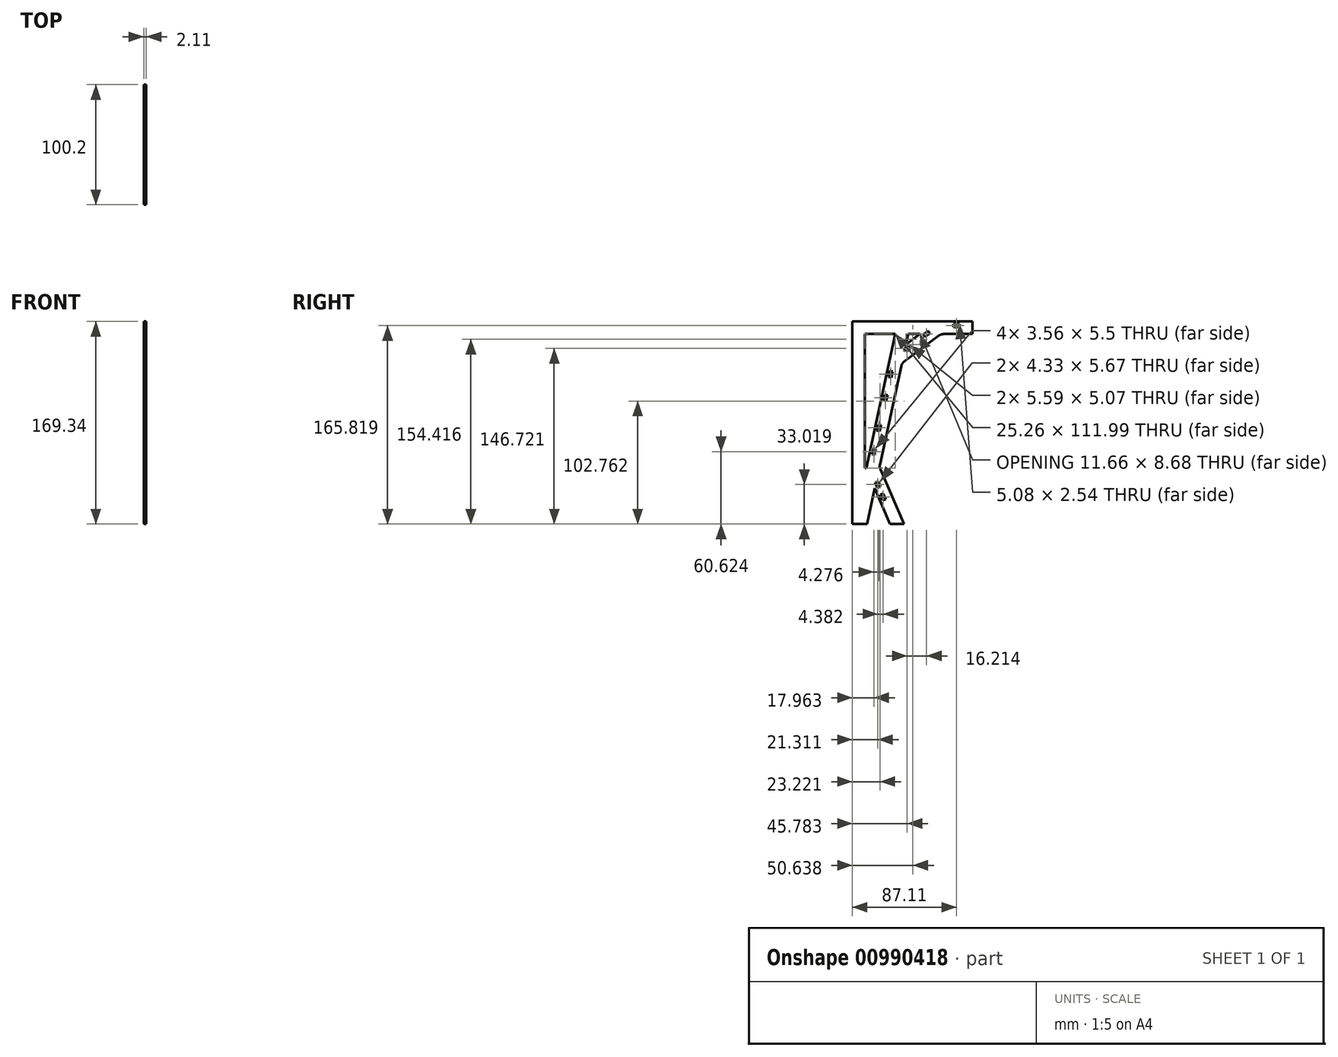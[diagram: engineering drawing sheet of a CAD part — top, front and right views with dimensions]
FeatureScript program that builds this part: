
annotation { "Feature Type Name" : "Feature", "Feature Type Description" : "" }
export const myFeature = defineFeature(function(context is Context, id is Id, definition is map)
    precondition{}
    {
        {
            var Q0;
            Q0=qCreatedBy(makeId("Right.planeOp"),FACE);
            var sketch = newSketch(context, id + "F0", { "sketchPlane" : qUnion([Q0])});
            skLineSegment(sketch, "E0", {"start": v(0, 0) * mm, "end": v(0, 169.34) * mm});
            skLineSegment(sketch, "E1", {"start": v(0, 169.34) * mm, "end": v(200.4, 169.34) * mm});
            skLineSegment(sketch, "E2", {"start": v(0, 0) * mm, "end": v(43.05, 0) * mm, "construction": true});
            skLineSegment(sketch, "E3", {"start": v(43.05, 0) * mm, "end": v(23.47, 45.96) * mm});
            skLineSegment(sketch, "E4", {"start": v(0, 47.82) * mm, "end": v(22.68, 47.82) * mm, "construction": true});
            skLineSegment(sketch, "E5", {"start": v(22.68, 47.82) * mm, "end": v(22.68, 0) * mm, "construction": true});
            skLineSegment(sketch, "E6", {"start": v(23.1, 49.8) * mm, "end": v(40.9, 132) * mm});
            skLineSegment(sketch, "E7", {"start": v(41.4, 134.33) * mm, "end": v(0, 134.33) * mm, "construction": true});
            skLineSegment(sketch, "E8", {"start": v(41.4, 134.33) * mm, "end": v(43.05, 0) * mm, "construction": true});
            skLineSegment(sketch, "E9", {"start": v(43.31, 135.75) * mm, "end": v(72.51, 157.5) * mm});
            skLineSegment(sketch, "E10", {"start": v(74.2, 158.76) * mm, "end": v(74.2, 169.34) * mm, "construction": true});
            skLineSegment(sketch, "E11", {"start": v(74.2, 158.76) * mm, "end": v(0, 158.76) * mm, "construction": true});
            skPoint(sketch, "E12", {"position": v(100.2, 169.34) * mm});
            skLineSegment(sketch, "E13", {"start": v(100.2, 169.34) * mm, "end": v(100.2, 154.3) * mm, "construction": true});
            skLineSegment(sketch, "E14", {"start": v(76.3, 158.76) * mm, "end": v(100.2, 158.76) * mm});
            skLineSegment(sketch, "E15.4", {"start": v(41.18, -0.8) * mm, "end": v(20.56, 47.62) * mm, "construction": true});
            skLineSegment(sketch, "E15.5", {"start": v(20.56, 47.62) * mm, "end": v(39.58, 135.5) * mm});
            skLineSegment(sketch, "E15.6", {"start": v(39.58, 135.5) * mm, "end": v(73.52, 160.79) * mm});
            skLineSegment(sketch, "E15.7", {"start": v(73.52, 160.79) * mm, "end": v(100.2, 160.79) * mm});
            skLineSegment(sketch, "E16.5", {"start": v(11.62, 46.77) * mm, "end": v(31.89, 140.45) * mm});
            skLineSegment(sketch, "E16.6", {"start": v(31.89, 140.45) * mm, "end": v(70.69, 169.35) * mm, "construction": true});
            skLineSegment(sketch, "E16.7", {"start": v(70.69, 169.35) * mm, "end": v(100.2, 169.35) * mm});
            skLineSegment(sketch, "E17", {"start": v(31.89, 140.45) * mm, "end": v(38.14, 169.34) * mm, "construction": true});
            skLineSegment(sketch, "E18", {"start": v(10.6, 158.76) * mm, "end": v(0, 158.76) * mm, "construction": true});
            skLineSegment(sketch, "E19", {"start": v(10.6, 158.76) * mm, "end": v(10.6, 46.77) * mm});
            skLineSegment(sketch, "E20", {"start": v(10.6, 46.77) * mm, "end": v(11.62, 46.77) * mm});
            skLineSegment(sketch, "E21", {"start": v(36.3, 160.79) * mm, "end": v(31.89, 140.45) * mm, "construction": true});
            skLineSegment(sketch, "E22", {"start": v(41.4, 134.33) * mm, "end": v(48.98, 169.34) * mm, "construction": true});
            skLineSegment(sketch, "E23", {"start": v(47.13, 160.79) * mm, "end": v(44.8, 150.07) * mm});
            skLineSegment(sketch, "E24", {"start": v(13.2, 0) * mm, "end": v(0, 0) * mm});
            skLineSegment(sketch, "E25", {"start": v(31.54, 0) * mm, "end": v(43.05, 0) * mm});
            skLineSegment(sketch, "E26", {"start": v(100.2, 158.76) * mm, "end": v(100.2, 169.35) * mm});
            skPoint(sketch, "E27", {"position": v(46.69, 158.76) * mm});
            skPoint(sketch, "E28", {"position": v(56.47, 158.76) * mm});
            skLineSegment(sketch, "E29", {"start": v(46.69, 158.76) * mm, "end": v(56.47, 158.76) * mm});
            skLineSegment(sketch, "E30", {"start": v(44.8, 150.07) * mm, "end": v(46.69, 158.76) * mm});
            skLineSegment(sketch, "E31", {"start": v(10.6, 158.76) * mm, "end": v(35.85, 158.76) * mm});
            skLineSegment(sketch, "E32", {"start": v(35.85, 158.76) * mm, "end": v(31.89, 140.45) * mm});
            skLineSegment(sketch, "E33", {"start": v(44.8, 150.07) * mm, "end": v(56.47, 158.76) * mm});
            skLineSegment(sketch, "E34", {"start": v(30.88, 85.7) * mm, "end": v(20.53, 87.94) * mm, "construction": true});
            skLineSegment(sketch, "E35.0", {"start": v(33.3, -4.15) * mm, "end": v(12.94, 43.67) * mm, "construction": true});
            skLineSegment(sketch, "E36", {"start": v(22.68, 47.82) * mm, "end": v(18.8, 29.9) * mm, "construction": true});
            skLineSegment(sketch, "E37", {"start": v(18.8, 29.9) * mm, "end": v(12.34, 0) * mm});
            skLineSegment(sketch, "E38", {"start": v(18.8, 29.9) * mm, "end": v(31.54, 0) * mm});
            skLineSegment(sketch, "E39", {"start": v(12.34, 0) * mm, "end": v(31.54, 0) * mm});
            skLineSegment(sketch, "E40", {"start": v(20.56, 47.62) * mm, "end": v(40.84, 0) * mm});
            skPoint(sketch, "E41.visualSharp", {"position": v(41.4, 134.33) * mm});
            skArc(sketch, "E41.filletArc", {"start": v(43.31, 135.75) * mm, "mid": v(41.77, 134.1) * mm, "end": v(40.9, 132) * mm});
            skPoint(sketch, "E42.visualSharp", {"position": v(22.68, 47.82) * mm});
            skArc(sketch, "E42.filletArc", {"start": v(23.1, 49.8) * mm, "mid": v(23, 47.85) * mm, "end": v(23.47, 45.96) * mm});
            skPoint(sketch, "E43.visualSharp", {"position": v(74.2, 158.76) * mm});
            skArc(sketch, "E43.filletArc", {"start": v(76.3, 158.76) * mm, "mid": v(74.3, 158.44) * mm, "end": v(72.51, 157.5) * mm});
            skPoint(sketch, "E44", {"position": v(21.75, 93.6) * mm});
            skLineSegment(sketch, "E45", {"start": v(21.75, 93.6) * mm, "end": v(22.1, 95.21) * mm});
            skLineSegment(sketch, "E46", {"start": v(22.1, 95.21) * mm, "end": v(26.54, 94.25) * mm});
            skLineSegment(sketch, "E47", {"start": v(29.56, 96.2) * mm, "end": v(37.5, 132.86) * mm});
            skLineSegment(sketch, "E48", {"start": v(35.55, 135.88) * mm, "end": v(31.1, 136.84) * mm});
            skPoint(sketch, "E49.visualSharp", {"position": v(38.03, 135.35) * mm});
            skArc(sketch, "E49.filletArc", {"start": v(37.5, 132.86) * mm, "mid": v(37.15, 134.78) * mm, "end": v(35.55, 135.88) * mm});
            skPoint(sketch, "E50.visualSharp", {"position": v(29.02, 93.72) * mm});
            skArc(sketch, "E50.filletArc", {"start": v(26.54, 94.25) * mm, "mid": v(28.45, 94.6) * mm, "end": v(29.56, 96.2) * mm});
            skLineSegment(sketch, "E51", {"start": v(21.75, 93.6) * mm, "end": v(32.1, 91.37) * mm, "construction": true});
            skLineSegment(sketch, "E52.0", {"start": v(35.01, 133.4) * mm, "end": v(30.57, 134.36) * mm});
            skLineSegment(sketch, "E52.1", {"start": v(22.64, 97.7) * mm, "end": v(27.08, 96.74) * mm});
            skLineSegment(sketch, "E52.2", {"start": v(27.08, 96.74) * mm, "end": v(27.08, 96.74) * mm});
            skLineSegment(sketch, "E52.3", {"start": v(27.08, 96.74) * mm, "end": v(35.01, 133.4) * mm});
            skLineSegment(sketch, "E52.4", {"start": v(35.01, 133.4) * mm, "end": v(35.01, 133.4) * mm});
            skLineSegment(sketch, "E53.MirrorCS", {"start": v(21.4, 92) * mm, "end": v(25.85, 91.04) * mm});
            skArc(sketch, "E54.MirrorCS", {"start": v(25.85, 91.04) * mm, "mid": v(27.44, 89.94) * mm, "end": v(27.8, 88.02) * mm});
            skLineSegment(sketch, "E55.MirrorCS", {"start": v(27.8, 88.02) * mm, "end": v(19.86, 51.36) * mm});
            skArc(sketch, "E56.MirrorCS", {"start": v(19.86, 51.36) * mm, "mid": v(18.75, 49.76) * mm, "end": v(16.84, 49.41) * mm});
            skLineSegment(sketch, "E57.MirrorCS", {"start": v(16.84, 49.41) * mm, "end": v(12.4, 50.38) * mm});
            skLineSegment(sketch, "E58.MirrorCS", {"start": v(17.37, 51.9) * mm, "end": v(12.94, 52.86) * mm});
            skLineSegment(sketch, "E59.MirrorCS", {"start": v(25.3, 88.56) * mm, "end": v(17.37, 51.9) * mm});
            skLineSegment(sketch, "E60.MirrorCS", {"start": v(20.87, 89.52) * mm, "end": v(25.3, 88.56) * mm});
            skLineSegment(sketch, "E61", {"start": v(33.72, 127.42) * mm, "end": v(31.23, 127.96) * mm});
            skLineSegment(sketch, "E62", {"start": v(31.23, 127.96) * mm, "end": v(30.16, 123) * mm});
            skLineSegment(sketch, "E63", {"start": v(30.16, 123) * mm, "end": v(32.64, 122.46) * mm});
            skLineSegment(sketch, "E64", {"start": v(28.37, 102.7) * mm, "end": v(25.88, 103.24) * mm});
            skLineSegment(sketch, "E65", {"start": v(25.88, 103.24) * mm, "end": v(26.96, 108.2) * mm});
            skLineSegment(sketch, "E66", {"start": v(26.96, 108.2) * mm, "end": v(29.44, 107.66) * mm});
            skLineSegment(sketch, "E67.MirrorCS", {"start": v(24.02, 82.6) * mm, "end": v(21.54, 83.13) * mm});
            skLineSegment(sketch, "E68.MirrorCS", {"start": v(21.54, 83.13) * mm, "end": v(20.46, 78.17) * mm});
            skLineSegment(sketch, "E69.MirrorCS", {"start": v(20.46, 78.17) * mm, "end": v(22.94, 77.63) * mm});
            skLineSegment(sketch, "E70.MirrorCS", {"start": v(17.26, 63.37) * mm, "end": v(19.74, 62.84) * mm});
            skLineSegment(sketch, "E71.MirrorCS", {"start": v(16.19, 58.4) * mm, "end": v(17.26, 63.37) * mm});
            skLineSegment(sketch, "E72.MirrorCS", {"start": v(18.67, 57.87) * mm, "end": v(16.19, 58.4) * mm});
            skLineSegment(sketch, "E73", {"start": v(31.89, 140.45) * mm, "end": v(41.4, 134.33) * mm, "construction": true});
            skLineSegment(sketch, "E74.MirrorCS", {"start": v(37.56, 139.02) * mm, "end": v(34.85, 142.66) * mm});
            skArc(sketch, "E75.MirrorCS", {"start": v(41.12, 138.5) * mm, "mid": v(39.23, 138.02) * mm, "end": v(37.56, 139.02) * mm});
            skLineSegment(sketch, "E76.MirrorCS", {"start": v(71.2, 160.9) * mm, "end": v(41.12, 138.5) * mm});
            skArc(sketch, "E77.MirrorCS", {"start": v(71.72, 164.46) * mm, "mid": v(72.2, 162.57) * mm, "end": v(71.2, 160.9) * mm});
            skLineSegment(sketch, "E78.MirrorCS", {"start": v(69, 168.1) * mm, "end": v(71.72, 164.46) * mm});
            skLineSegment(sketch, "E79.MirrorCS", {"start": v(66.97, 166.58) * mm, "end": v(69.69, 162.94) * mm});
            skLineSegment(sketch, "E80.MirrorCS", {"start": v(69.69, 162.94) * mm, "end": v(39.6, 140.53) * mm});
            skLineSegment(sketch, "E81.MirrorCS", {"start": v(64.8, 159.3) * mm, "end": v(63.28, 161.33) * mm});
            skLineSegment(sketch, "E82.MirrorCS", {"start": v(63.28, 161.33) * mm, "end": v(59.2, 158.3) * mm});
            skLineSegment(sketch, "E83.MirrorCS", {"start": v(59.2, 158.3) * mm, "end": v(60.72, 156.26) * mm});
            skLineSegment(sketch, "E84.MirrorCS", {"start": v(47.06, 149.26) * mm, "end": v(48.58, 147.22) * mm});
            skLineSegment(sketch, "E85.MirrorCS", {"start": v(42.99, 146.22) * mm, "end": v(47.06, 149.26) * mm});
            skLineSegment(sketch, "E86.MirrorCS", {"start": v(44.5, 144.19) * mm, "end": v(42.99, 146.22) * mm});
            skLineSegment(sketch, "E87.MirrorCS", {"start": v(39.6, 140.53) * mm, "end": v(36.89, 144.18) * mm});
            skLineSegment(sketch, "E88", {"start": v(70.69, 169.35) * mm, "end": v(70.69, 164.55) * mm});
            skLineSegment(sketch, "E89", {"start": v(68.15, 162) * mm, "end": v(0, 162) * mm});
            skPoint(sketch, "E90.visualSharp", {"position": v(70.69, 162) * mm});
            skArc(sketch, "E90.filletArc", {"start": v(68.15, 162) * mm, "mid": v(69.94, 162.75) * mm, "end": v(70.69, 164.55) * mm});
            skLineSegment(sketch, "E91.0", {"start": v(68.15, 164.55) * mm, "end": v(0, 164.55) * mm});
            skLineSegment(sketch, "E91.1", {"start": v(68.15, 169.63) * mm, "end": v(68.15, 164.55) * mm});
            skLineSegment(sketch, "E92", {"start": v(55.17, 164.55) * mm, "end": v(55.17, 167.09) * mm});
            skLineSegment(sketch, "E93", {"start": v(55.17, 167.09) * mm, "end": v(50.1, 167.09) * mm});
            skLineSegment(sketch, "E94", {"start": v(50.1, 167.09) * mm, "end": v(50.1, 164.55) * mm});
            skLineSegment(sketch, "E95", {"start": v(10.4, 164.55) * mm, "end": v(10.4, 167.09) * mm});
            skLineSegment(sketch, "E96", {"start": v(10.4, 167.09) * mm, "end": v(5.32, 167.09) * mm});
            skLineSegment(sketch, "E97", {"start": v(5.32, 167.09) * mm, "end": v(5.32, 164.55) * mm});
            skLineSegment(sketch, "E98", {"start": v(22.68, 47.82) * mm, "end": v(11.62, 46.77) * mm, "construction": true});
            skLineSegment(sketch, "E99", {"start": v(15.36, 37.97) * mm, "end": v(19.78, 39.85) * mm});
            skLineSegment(sketch, "E100", {"start": v(23.11, 38.51) * mm, "end": v(37.3, 5.2) * mm});
            skLineSegment(sketch, "E101", {"start": v(35.96, 1.87) * mm, "end": v(31.54, -0.01) * mm});
            skPoint(sketch, "E102.visualSharp", {"position": v(38.3, 2.87) * mm});
            skArc(sketch, "E102.filletArc", {"start": v(35.96, 1.87) * mm, "mid": v(37.32, 3.26) * mm, "end": v(37.3, 5.2) * mm});
            skPoint(sketch, "E103.visualSharp", {"position": v(22.12, 40.85) * mm});
            skArc(sketch, "E103.filletArc", {"start": v(23.11, 38.51) * mm, "mid": v(21.72, 39.87) * mm, "end": v(19.78, 39.85) * mm});
            skLineSegment(sketch, "E104.0", {"start": v(34.97, 4.2) * mm, "end": v(25.52, 0.18) * mm});
            skLineSegment(sketch, "E104.1", {"start": v(20.78, 37.52) * mm, "end": v(34.97, 4.2) * mm});
            skLineSegment(sketch, "E104.2", {"start": v(16.36, 35.63) * mm, "end": v(20.78, 37.52) * mm});
            skLineSegment(sketch, "E105", {"start": v(27.86, 20.9) * mm, "end": v(25.52, 19.9) * mm});
            skLineSegment(sketch, "E106", {"start": v(25.52, 19.9) * mm, "end": v(23.53, 24.57) * mm});
            skLineSegment(sketch, "E107", {"start": v(23.53, 24.57) * mm, "end": v(25.87, 25.57) * mm});
            skLineSegment(sketch, "E108", {"start": v(21.48, 35.85) * mm, "end": v(19.15, 34.86) * mm});
            skLineSegment(sketch, "E109", {"start": v(19.15, 34.86) * mm, "end": v(21.14, 30.18) * mm});
            skLineSegment(sketch, "E110", {"start": v(21.14, 30.18) * mm, "end": v(23.48, 31.18) * mm});
            skLineSegment(sketch, "E111", {"start": v(79.6, 169.35) * mm, "end": v(79.6, 164.55) * mm});
            skLineSegment(sketch, "E112", {"start": v(82.14, 162) * mm, "end": v(100.2, 162) * mm});
            skPoint(sketch, "E113.visualSharp", {"position": v(79.6, 162) * mm});
            skArc(sketch, "E113.filletArc", {"start": v(79.6, 164.55) * mm, "mid": v(80.34, 162.75) * mm, "end": v(82.14, 162) * mm});
            skLineSegment(sketch, "E114.0", {"start": v(82.14, 164.55) * mm, "end": v(100.2, 164.55) * mm});
            skLineSegment(sketch, "E114.1", {"start": v(82.14, 169.35) * mm, "end": v(82.14, 164.55) * mm});
            skLineSegment(sketch, "E115", {"start": v(84.57, 164.55) * mm, "end": v(84.57, 167.09) * mm});
            skPoint(sketch, "E115.endSnap0", {"position": v(68.15, 167.09) * mm});
            skLineSegment(sketch, "E116", {"start": v(84.57, 167.09) * mm, "end": v(89.65, 167.09) * mm});
            skLineSegment(sketch, "E117", {"start": v(89.65, 167.09) * mm, "end": v(89.65, 164.55) * mm});
            skSolve(sketch);
        }
        {
            var Q0;
            Q0=makeQuery(id+"F0.imprint","IMPRINT",FACE,{"disambiguationData":[TD([[makeQuery(id+"F0.imprint","IMPRINT",EDGE,{"derivedFrom":sQuery(id+"F0.wireOp",EDGE,"E15.5")}),1.0]])]});
            var Q1;
            {var subQ0=sQuery(id+"F0.wireOp",EDGE,"E92");Q1=makeQuery(id+"F0.imprint","IMPRINT",FACE,{"disambiguationData":[TD([[makeQuery(id+"F0.imprint","IMPRINT",EDGE,{"derivedFrom":subQ0}),-1.0]])]});}
            var Q2;
            {var subQ10=sQuery(id+"F0.wireOp",EDGE,"E89");Q2=makeQuery(id+"F0.imprint","IMPRINT",FACE,{"disambiguationData":[TD([[makeQuery(id+"F0.imprint","IMPRINT",EDGE,{"derivedFrom":subQ10}),-1.0]])]});}
            var Q3;
            {var subQ0=sQuery(id+"F0.wireOp",EDGE,"E88");var subQ1=makeQuery(id+"F0.imprint","IMPRINT",VERTEX,{"derivedFrom":subQ0});Q3=makeQuery(id+"F0.imprint","IMPRINT",FACE,{"disambiguationData":[TD([[makeQuery(id+"F0.imprint","IMPRINT",EDGE,{"disambiguationData":[TD([[subQ1,1.0]])],"derivedFrom":subQ0}),-1.0]])]});}
            var Q4;
            {var subQ3=sQuery(id+"F0.wireOp",EDGE,"E115");Q4=makeQuery(id+"F0.imprint","IMPRINT",FACE,{"disambiguationData":[TD([[makeQuery(id+"F0.imprint","IMPRINT",EDGE,{"derivedFrom":subQ3}),1.0]])]});}
            var Q5;
            {var subQ4=sQuery(id+"F0.wireOp",EDGE,"E112");Q5=makeQuery(id+"F0.imprint","IMPRINT",FACE,{"disambiguationData":[TD([[makeQuery(id+"F0.imprint","IMPRINT",EDGE,{"derivedFrom":subQ4}),1.0]])]});}
            var Q6;
            {var subQ2=sQuery(id+"F0.wireOp",EDGE,"E3");Q6=makeQuery(id+"F0.imprint","IMPRINT",FACE,{"disambiguationData":[TD([[makeQuery(id+"F0.imprint","IMPRINT",EDGE,{"derivedFrom":subQ2}),1.0]])]});}
            var Q7;
            {var subQ5=sQuery(id+"F0.wireOp",EDGE,"E46");Q7=makeQuery(id+"F0.imprint","IMPRINT",FACE,{"disambiguationData":[TD([[makeQuery(id+"F0.imprint","IMPRINT",EDGE,{"derivedFrom":subQ5}),1.0]])]});}
            var Q8;
            {var subQ3=sQuery(id+"F0.wireOp",EDGE,"E52.0");Q8=makeQuery(id+"F0.imprint","IMPRINT",FACE,{"disambiguationData":[TD([[makeQuery(id+"F0.imprint","IMPRINT",EDGE,{"derivedFrom":subQ3}),1.0]])]});}
            var Q9;
            {var subQ7=sQuery(id+"F0.wireOp",EDGE,"E53.MirrorCS");Q9=makeQuery(id+"F0.imprint","IMPRINT",FACE,{"disambiguationData":[TD([[makeQuery(id+"F0.imprint","IMPRINT",EDGE,{"derivedFrom":subQ7}),-1.0]])]});}
            var Q10;
            {var subQ4=sQuery(id+"F0.wireOp",EDGE,"E58.MirrorCS");Q10=makeQuery(id+"F0.imprint","IMPRINT",FACE,{"disambiguationData":[TD([[makeQuery(id+"F0.imprint","IMPRINT",EDGE,{"derivedFrom":subQ4}),-1.0]])]});}
            var Q11;
            {var subQ0=sQuery(id+"F0.wireOp",EDGE,"E95");Q11=makeQuery(id+"F0.imprint","IMPRINT",FACE,{"disambiguationData":[TD([[makeQuery(id+"F0.imprint","IMPRINT",EDGE,{"derivedFrom":subQ0}),1.0]])]});}
            var Q12;
            {var subQ0=sQuery(id+"F0.wireOp",EDGE,"E92");Q12=makeQuery(id+"F0.imprint","IMPRINT",FACE,{"disambiguationData":[TD([[makeQuery(id+"F0.imprint","IMPRINT",EDGE,{"derivedFrom":subQ0}),1.0]])]});}
            extrude(context, id + "F1", {"entities" : qUnion([Q0, Q1, Q2, Q3, Q4, Q5, Q6, Q7, Q8, Q9, Q10, Q11, Q12]), "depth" : 2.1 * mm, "offsetDistance" : 25.4 * mm});
        }
        {
            var Q0;
            Q0=makeQuery(id+"F1.opExtrude","CAP_EDGE",EDGE,{"disambiguationData":[OSD([sQuery(id+"F0.wireOp",EDGE,"E9")])],"isStart":true});
            fillet(context, id + "F2", {"entities" : qUnion([Q0]), "radius" : 0.76 * mm, "tangentPropagation" : true, "allowEdgeOverflow" : false});
        }
    });
